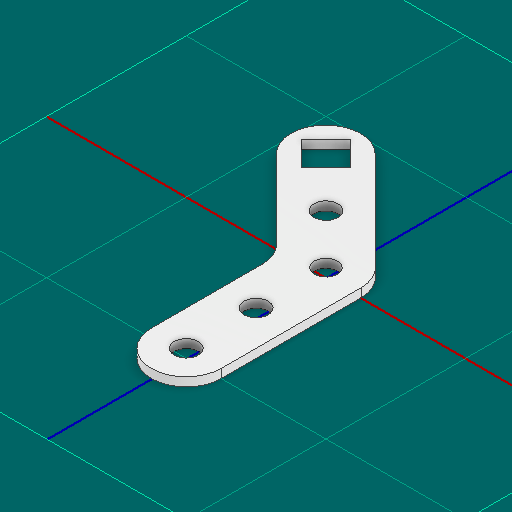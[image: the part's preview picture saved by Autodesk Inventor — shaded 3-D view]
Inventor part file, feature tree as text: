
AUTODESK INVENTOR PART (.ipt)
format: ipt  version: 2025 (Build 290162000, 162)  size: 139,776 bytes
history: native  units: in
note: dims shown in document units (in); Inventor stores cm internally (conversion verified against a paired STEP export)
features: other x5, sketch x1
ambient origin geometry x8: Origin, YZ Plane, XZ Plane, XY Plane, X Axis, Y Axis, Z Axis, Center Point
bodies: Solid1 (feature_tree)
feature tree (6):
  other  "gusset.ipt"
  other  "Blocks"
  other  "main"
  other  "Solid1::gusset.ipt"
  other  "TaggingFeature1"
  sketch  "Sketch1"  dims[d0=0.3937in d5=0.5in d6=0.25in d9=0.248in d10=45.0deg d11=0.248in]
